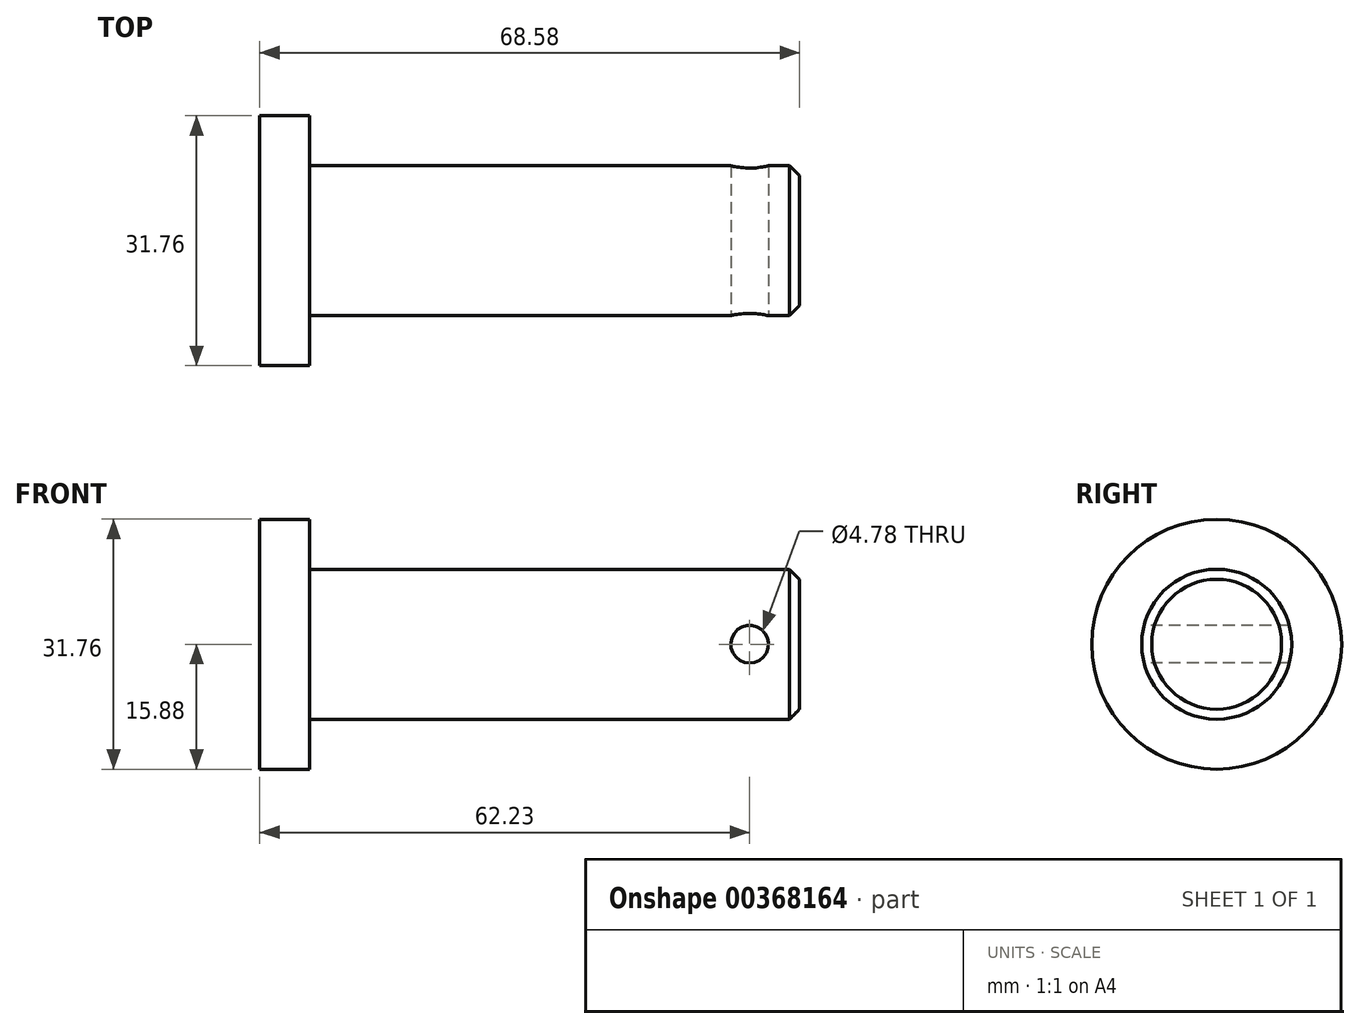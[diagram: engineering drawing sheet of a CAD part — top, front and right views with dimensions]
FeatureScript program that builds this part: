
annotation { "Feature Type Name" : "Feature", "Feature Type Description" : "" }
export const myFeature = defineFeature(function(context is Context, id is Id, definition is map)
    precondition{}
    {
        {
            var Q0;
            Q0=qCreatedBy(makeId("Right.planeOp"),FACE);
            var sketch = newSketch(context, id + "F0", { "sketchPlane" : qUnion([Q0])});
            skCircle(sketch, "E0", {"center": v(0, 0) * mm, "radius": 15.88 * mm});
            skSolve(sketch);
        }
        {
            var Q0;
            Q0 = qSketchRegion(id + "F0", true);
            extrude(context, id + "F1", {"entities" : qUnion([Q0]), "depth" : 6.35 * mm});
        }
        {
            var Q0;
            Q0=makeQuery(id+"F1.opExtrude","CAP_FACE",FACE,{"disambiguationData":[OSD([sQuery(id+"F0.wireOp",EDGE,"E0")])],"isStart":false});
            var sketch = newSketch(context, id + "F2", { "sketchPlane" : qUnion([Q0])});
            skCircle(sketch, "E1", {"center": v(0, 0) * mm, "radius": 9.53 * mm});
            skSolve(sketch);
        }
        {
            var Q0;
            Q0 = qSketchRegion(id + "F2", true);
            extrude(context, id + "F3", {"entities" : qUnion([Q0]), "operationType" : NewBodyOperationType.ADD, "depth" : 62.23 * mm});
        }
        {
            var Q0;
            Q0=qCreatedBy(makeId("Front.planeOp"),FACE);
            cPlane(context, id + "F4", {"entities" : qUnion([Q0]), "cplaneType" : CPlaneType.OFFSET, "offset" : 9.52 * mm, "width" : 152.4 * mm, "height" : 152.4 * mm});
        }
        {
            var Q0;
            Q0=qCreatedBy(id+"F4.planeOp",FACE);
            var sketch = newSketch(context, id + "F5", { "sketchPlane" : qUnion([Q0])});
            skCircle(sketch, "E2", {"center": v(62.23, 0) * mm, "radius": 2.39 * mm});
            skSolve(sketch);
        }
        {
            var Q0;
            Q0 = qSketchRegion(id + "F5", true);
            extrude(context, id + "F6", {"entities" : qUnion([Q0]), "operationType" : NewBodyOperationType.REMOVE, "endBound" : BoundingType.THROUGH_ALL, "oppositeDirection" : true, "depth" : 25.4 * mm});
        }
        {
            var Q0;
            Q0=makeQuery(id+"F3.opExtrude","CAP_EDGE",EDGE,{"disambiguationData":[OSD([sQuery(id+"F2.wireOp",EDGE,"E1")])],"isStart":false});
            chamfer(context, id + "F7", {"entities" : qUnion([Q0]), "chamferType" : ChamferType.OFFSET_ANGLE, "width" : 1.27 * mm, "oppositeDirection" : false, "angle" : 45 * degree, "tangentPropagation" : true});
        }
    });
